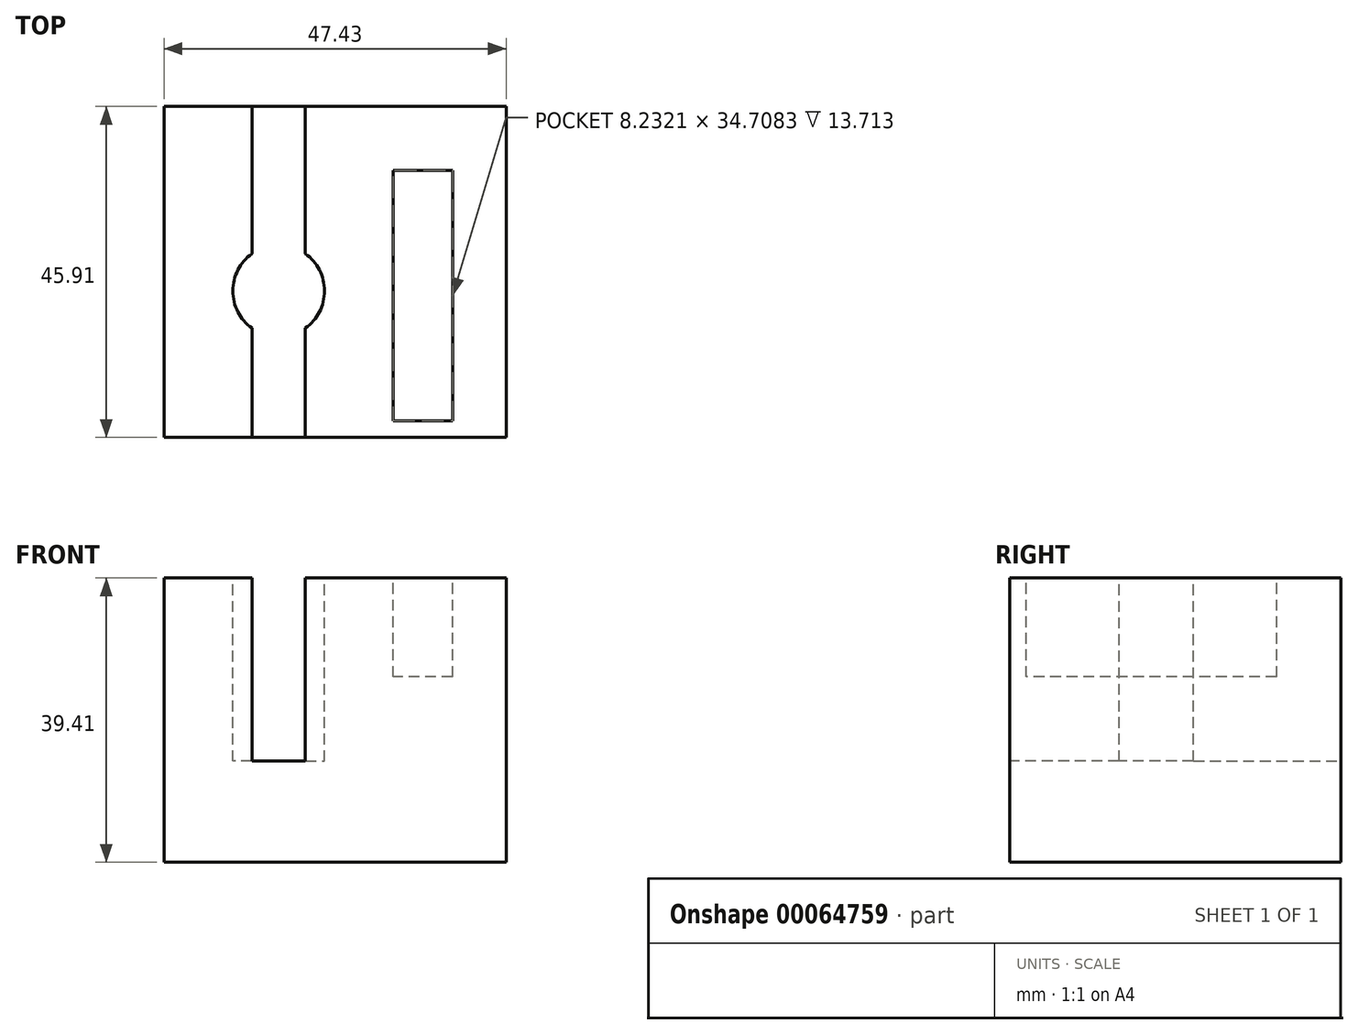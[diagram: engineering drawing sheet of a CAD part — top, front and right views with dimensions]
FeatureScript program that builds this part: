
annotation { "Feature Type Name" : "Feature", "Feature Type Description" : "" }
export const myFeature = defineFeature(function(context is Context, id is Id, definition is map)
    precondition{}
    {
        {
            var Q0;
            Q0=qCreatedBy(makeId("Top.planeOp"),FACE);
            var sketch = newSketch(context, id + "F0", { "sketchPlane" : qUnion([Q0])});
            skLineSegment(sketch, "E0.bottom", {"start": v(0, 0) * mm, "end": v(47.43, 0) * mm});
            skLineSegment(sketch, "E0.top", {"start": v(0, 45.91) * mm, "end": v(47.43, 45.91) * mm});
            skLineSegment(sketch, "E0.left", {"start": v(0, 0) * mm, "end": v(0, 45.91) * mm});
            skLineSegment(sketch, "E0.right", {"start": v(47.43, 0) * mm, "end": v(47.43, 45.91) * mm});
            skSolve(sketch);
        }
        {
            var Q0;
            Q0 = qSketchRegion(id + "F0", true);
            var Q1;
            Q1=makeQuery(id+"F0.imprint","IMPRINT",FACE,{"disambiguationData":[TD([[makeQuery(id+"F0.imprint","IMPRINT",EDGE,{"derivedFrom":sQuery(id+"F0.wireOp",EDGE,"E0.bottom")}),1.0]])]});
            extrude(context, id + "F1", {"entities" : qUnion([Q0, Q1]), "depth" : 39.4 * mm});
        }
        {
            var Q0;
            Q0=makeQuery(id+"F1.opExtrude","CAP_FACE",FACE,{"disambiguationData":[OSD([sQuery(id+"F0.wireOp",EDGE,"E0.bottom"),sQuery(id+"F0.wireOp",EDGE,"E0.top"),sQuery(id+"F0.wireOp",EDGE,"E0.left"),sQuery(id+"F0.wireOp",EDGE,"E0.right")])],"isStart":false});
            var sketch = newSketch(context, id + "F2", { "sketchPlane" : qUnion([Q0])});
            skLineSegment(sketch, "E1.bottom", {"start": v(40, 37) * mm, "end": v(31.77, 37) * mm});
            skLineSegment(sketch, "E1.top", {"start": v(40, 2.3) * mm, "end": v(31.77, 2.3) * mm});
            skLineSegment(sketch, "E1.left", {"start": v(40, 37) * mm, "end": v(40, 2.3) * mm});
            skLineSegment(sketch, "E1.right", {"start": v(31.77, 37) * mm, "end": v(31.77, 2.3) * mm});
            skSolve(sketch);
        }
        {
            var Q0;
            Q0=makeQuery(id+"F2.imprint","IMPRINT",FACE,{"disambiguationData":[TD([[makeQuery(id+"F2.imprint","IMPRINT",EDGE,{"derivedFrom":sQuery(id+"F2.wireOp",EDGE,"E1.bottom")}),1.0]])]});
            extrude(context, id + "F3", {"entities" : qUnion([Q0]), "operationType" : NewBodyOperationType.REMOVE, "oppositeDirection" : true, "depth" : 13.71 * mm});
        }
        {
            var Q0;
            Q0=makeQuery(id+"F1.opExtrude","CAP_FACE",FACE,{"disambiguationData":[OSD([sQuery(id+"F0.wireOp",EDGE,"E0.bottom"),sQuery(id+"F0.wireOp",EDGE,"E0.top"),sQuery(id+"F0.wireOp",EDGE,"E0.left"),sQuery(id+"F0.wireOp",EDGE,"E0.right")])],"isStart":false});
            var sketch = newSketch(context, id + "F4", { "sketchPlane" : qUnion([Q0])});
            skArc(sketch, "E2", {"start": v(12.2, 25.48) * mm, "mid": v(9.55, 20.32) * mm, "end": v(12.2, 15.16) * mm});
            skLineSegment(sketch, "E3.top", {"start": v(19.6, 45.91) * mm, "end": v(12.2, 45.91) * mm});
            skLineSegment(sketch, "E3.left", {"start": v(19.6, 25.48) * mm, "end": v(19.6, 45.91) * mm});
            skLineSegment(sketch, "E3.right", {"start": v(12.2, 25.48) * mm, "end": v(12.2, 45.91) * mm});
            skLineSegment(sketch, "E4.top", {"start": v(19.6, 0) * mm, "end": v(12.2, 0) * mm});
            skLineSegment(sketch, "E4.left", {"start": v(19.6, 15.16) * mm, "end": v(19.6, 0) * mm});
            skLineSegment(sketch, "E4.right", {"start": v(12.2, 15.16) * mm, "end": v(12.2, 0) * mm});
            skArc(sketch, "E5.trimOffspring", {"start": v(19.6, 15.16) * mm, "mid": v(22.25, 20.32) * mm, "end": v(19.6, 25.48) * mm});
            skSolve(sketch);
        }
        {
            var Q0;
            Q0 = qSketchRegion(id + "F4", true);
            extrude(context, id + "F5", {"entities" : qUnion([Q0]), "operationType" : NewBodyOperationType.REMOVE, "oppositeDirection" : true, "depth" : 25.4 * mm});
        }
        {
            var Q0;
            Q0=qCreatedBy(makeId("Top.planeOp"),FACE);
            cPlane(context, id + "F6", {"entities" : qUnion([Q0]), "cplaneType" : CPlaneType.OFFSET, "offset" : 20 * mm, "width" : 150 * mm, "height" : 150 * mm});
        }
        {
            var Q0;
            Q0=qCreatedBy(id+"F6.planeOp",FACE);
            var sketch = newSketch(context, id + "F7", { "sketchPlane" : qUnion([Q0])});
            skArc(sketch, "E6", {"start": v(0, -13.65) * mm, "mid": v(-24, -22.74) * mm, "end": v(-43.51, -39.43) * mm});
            skSolve(sketch);
        }
    });
